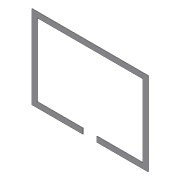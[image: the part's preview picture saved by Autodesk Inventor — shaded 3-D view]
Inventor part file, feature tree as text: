
AUTODESK INVENTOR PART (.ipt)
format: ipt  version: 2012 (Build 160160000, 160)  size: 82,944 bytes
history: native  units: in
note: dims shown in document units (in); Inventor stores cm internally (conversion verified against a paired STEP export)
features: extrude x2, sketch x2
ambient origin geometry x8: Origin, YZ Plane, XZ Plane, XY Plane, X Axis, Y Axis, Z Axis, Center Point
bodies: Solid1 (feature_tree)
feature tree (4):
  extrude  "Extrusion1"  Depth=44.0in
  extrude  "Extrusion2"  Depth=0.188in TaperAngle=0.0deg
  sketch  "Sketch1"  dims[d0=31.5in d1=44.0in]
  sketch  "Sketch2"  dims[d2=2.0in d3=0.188in d4=0.0in d5=5.25in d6=19.375in d7=1.0in d8=0.0in]
